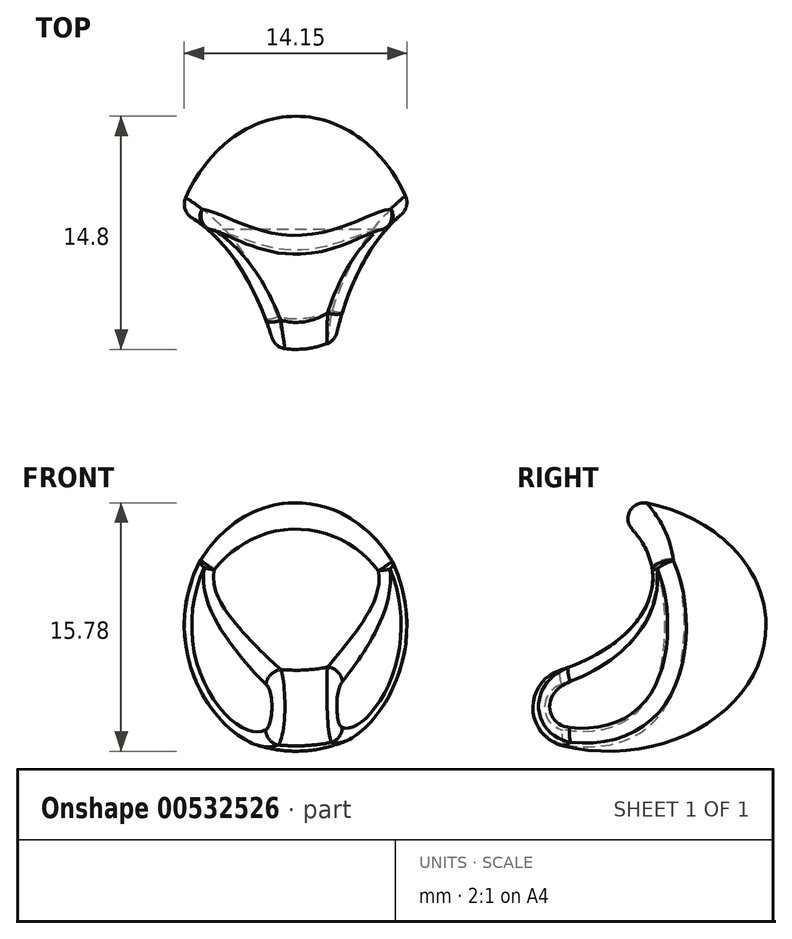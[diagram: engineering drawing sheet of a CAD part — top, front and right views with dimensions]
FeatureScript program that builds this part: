
annotation { "Feature Type Name" : "Feature", "Feature Type Description" : "" }
export const myFeature = defineFeature(function(context is Context, id is Id, definition is map)
    precondition{}
    {
        {
            var Q0;
            Q0=qCreatedBy(makeId("Right.planeOp"),FACE);
            var sketch = newSketch(context, id + "F0", { "sketchPlane" : qUnion([Q0])});
            skEllipticalArc(sketch, "E0", {});
            skLineSegment(sketch, "E1", {"start": v(0, 8) * mm, "end": v(0, 0) * mm, "construction": true});
            skLineSegment(sketch, "E2", {"start": v(0, 0) * mm, "end": v(-10, 0) * mm, "construction": true});
            skPoint(sketch, "E2.endSnap0", {"position": v(-10, 0) * mm});
            skLineSegment(sketch, "E3", {"start": v(0, 8) * mm, "end": v(-20, 8) * mm});
            const initialGuessF0  = {"E0": [-0.01, 0.008, -1, 0, 0.01, 0.008, 0, 3.141592653589793]};
            skSetInitialGuess(sketch, initialGuessF0);
            skSolve(sketch);
        }
        {
            var Q0;
            Q0=makeQuery(id+"F0.imprint","IMPRINT",FACE,{"disambiguationData":[TD([[makeQuery(id+"F0.imprint","IMPRINT",EDGE,{"derivedFrom":sQuery(id+"F0.wireOp",EDGE,"E0")}),1.0]])]});
            var Q1;
            Q1=sQuery(id+"F0.wireOp",EDGE,"E3");
            var Q2;
            Q2=sQuery(id+"F0.wireOp",EDGE,"E3");
            revolve(context, id + "F1", {"entities" : qUnion([Q0]), "surfaceEntities" : qUnion([Q1]), "axis" : qUnion([Q2]), "revolveType" : RevolveType.FULL});
        }
        {
            var Q0;
            Q0=qCreatedBy(makeId("Right.planeOp"),FACE);
            var sketch = newSketch(context, id + "F2", { "sketchPlane" : qUnion([Q0])});
            skEllipse(sketch, "E4", {"center": v(-19, 11) * mm, "majorRadius": 11.8 * mm, "minorRadius": 6.76 * mm, "majorAxis": v(-1, 0)});
            skSolve(sketch);
        }
        {
            var Q0;
            Q0 = qSketchRegion(id + "F2", true);
            extrude(context, id + "F3", {"entities" : qUnion([Q0]), "operationType" : NewBodyOperationType.REMOVE, "endBound" : BoundingType.SYMMETRIC, "oppositeDirection" : true, "depth" : 25 * mm, "offsetDistance" : 25 * mm});
        }
        {
            var Q0;
            Q0=qCreatedBy(makeId("Top.planeOp"),FACE);
            var sketch = newSketch(context, id + "F4", { "sketchPlane" : qUnion([Q0])});
            skEllipse(sketch, "E5", {"center": v(-9.7, -22) * mm, "majorRadius": 16.48 * mm, "minorRadius": 9.32 * mm, "majorAxis": v(0, 1)});
            skLineSegment(sketch, "E6", {"start": v(0, 0) * mm, "end": v(0.8, -22) * mm, "construction": true});
            skPoint(sketch, "E6.endSnap0", {"position": v(-0.38, -22) * mm});
            skEllipse(sketch, "E7.MirrorC", {"center": v(11.28, -21.23) * mm, "majorRadius": 16.48 * mm, "minorRadius": 9.32 * mm, "majorAxis": v(-0.07, 1)});
            skSolve(sketch);
        }
        {
            var Q0;
            Q0 = qSketchRegion(id + "F4", true);
            extrude(context, id + "F5", {"entities" : qUnion([Q0]), "operationType" : NewBodyOperationType.REMOVE, "endBound" : BoundingType.THROUGH_ALL, "depth" : 25 * mm, "offsetDistance" : 25 * mm});
        }
        {
            var Q0;
            Q0=makeQuery(id+"F5.boolean.opBoolean","SPLIT",EDGE,{"disambiguationData":[OD(1.0)],"derivedFrom":makeQuery(id+"F3.boolean.opBoolean","INTERSECT",EDGE,{"derivedFrom":[makeQuery(id+"F1.opRevolve","SWEPT_FACE",FACE,{"disambiguationData":[OSD([sQuery(id+"F0.wireOp",EDGE,"E0")])]}),makeQuery(id+"F3.opExtrude","SWEPT_FACE",FACE,{"disambiguationData":[OSD([sQuery(id+"F2.wireOp",EDGE,"E4")])]})]})});
            fillet(context, id + "F6", {"entities" : qUnion([Q0]), "radius" : 1 * mm, "tangentPropagation" : true, "allowEdgeOverflow" : false});
        }
        {
            var Q0;
            Q0=makeQuery(id+"F5.boolean.opBoolean","COPY",FACE,{"derivedFrom":makeQuery(id+"F5.opExtrude","SWEPT_FACE",FACE,{"disambiguationData":[OSD([sQuery(id+"F4.wireOp",EDGE,"E5")])]})});
            var Q1;
            Q1=makeQuery(id+"F5.boolean.opBoolean","COPY",FACE,{"derivedFrom":makeQuery(id+"F5.opExtrude","SWEPT_FACE",FACE,{"disambiguationData":[OSD([sQuery(id+"F4.wireOp",EDGE,"E7.MirrorC")])]})});
            fillet(context, id + "F7", {"entities" : qUnion([Q0, Q1]), "radius" : 1 * mm, "tangentPropagation" : true, "allowEdgeOverflow" : false});
        }
        {
            var Q0;
            Q0=makeQuery(id+"F3.boolean.opBoolean","INTERSECT",EDGE,{"derivedFrom":[makeQuery(id+"F1.opRevolve","SWEPT_FACE",FACE,{"disambiguationData":[OSD([sQuery(id+"F0.wireOp",EDGE,"E0")])]}),makeQuery(id+"F3.opExtrude","SWEPT_FACE",FACE,{"disambiguationData":[OSD([sQuery(id+"F2.wireOp",EDGE,"E4")])]})]});
            fillet(context, id + "F8", {"entities" : qUnion([Q0]), "radius" : 2.5 * mm, "tangentPropagation" : true, "allowEdgeOverflow" : false});
        }
    });
